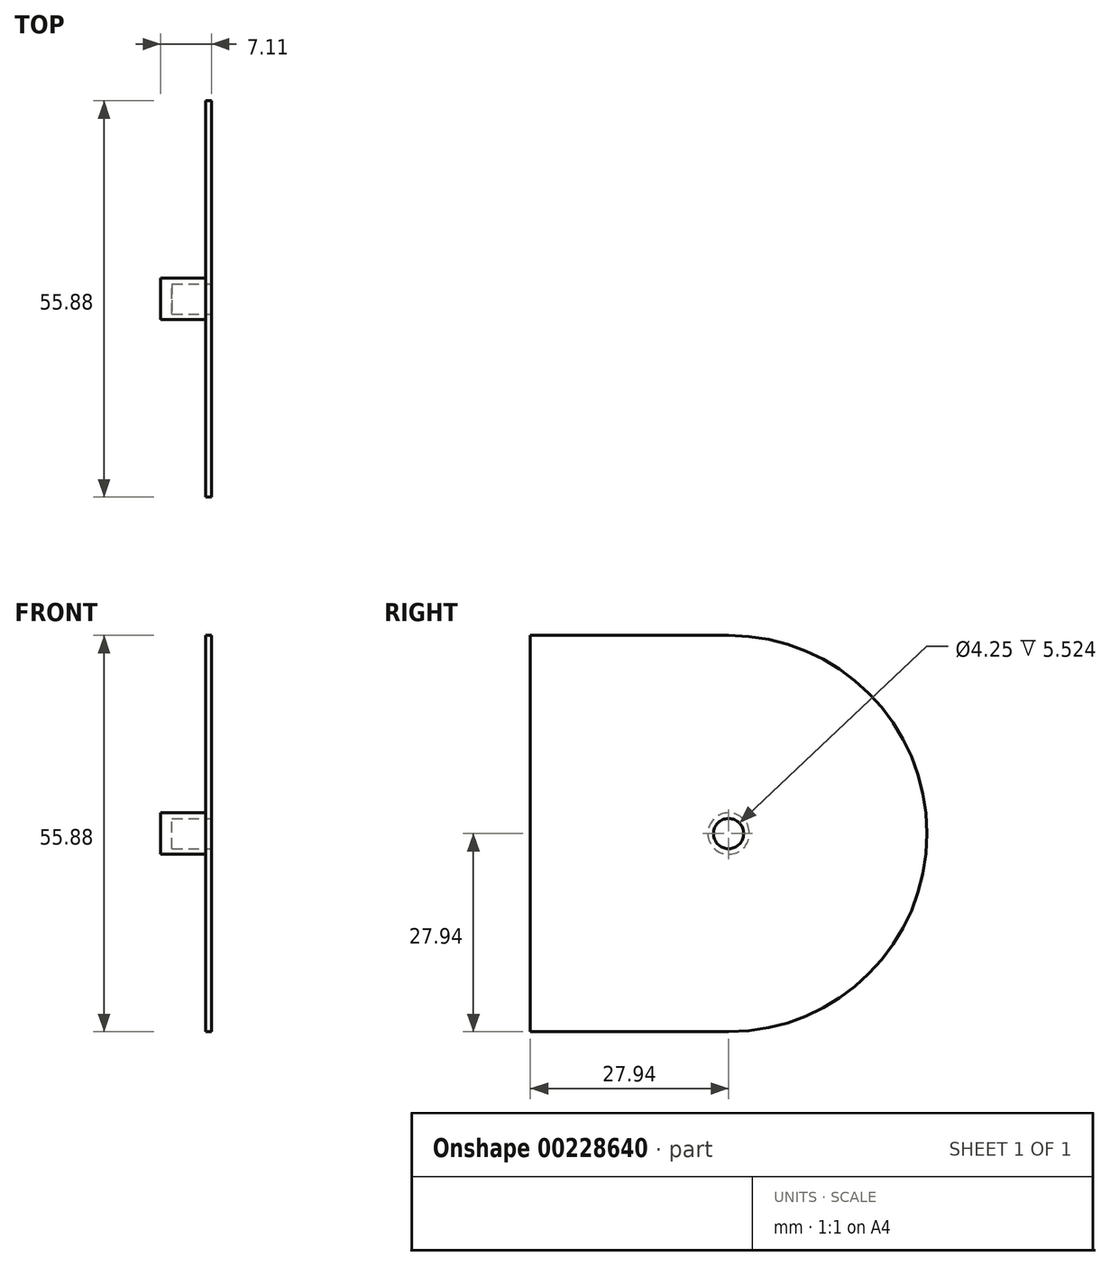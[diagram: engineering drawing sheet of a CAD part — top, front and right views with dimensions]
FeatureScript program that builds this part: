
annotation { "Feature Type Name" : "Feature", "Feature Type Description" : "" }
export const myFeature = defineFeature(function(context is Context, id is Id, definition is map)
    precondition{}
    {
        {
            var Q0;
            Q0=qCreatedBy(makeId("Right.planeOp"),FACE);
            var sketch = newSketch(context, id + "F0", { "sketchPlane" : qUnion([Q0])});
            skArc(sketch, "E0", {"start": v(0, -27.94) * mm, "mid": v(27.94, 0) * mm, "end": v(0, 27.94) * mm});
            skLineSegment(sketch, "E1", {"start": v(-27.94, 27.94) * mm, "end": v(-27.94, -27.94) * mm});
            skLineSegment(sketch, "E2", {"start": v(0, 27.94) * mm, "end": v(-27.94, 27.94) * mm});
            skLineSegment(sketch, "E3", {"start": v(0, -27.94) * mm, "end": v(-27.94, -27.94) * mm});
            skSolve(sketch);
        }
        {
            var Q0;
            Q0 = qSketchRegion(id + "F0", true);
            extrude(context, id + "F1", {"entities" : qUnion([Q0]), "depth" : 0.76 * mm, "offsetDistance" : 25.4 * mm});
        }
        {
            var Q0;
            Q0=makeQuery(id+"F1.opExtrude","CAP_FACE",FACE,{"disambiguationData":[OSD([sQuery(id+"F0.wireOp",EDGE,"vK9xomXJ-WcoS-fqkd-62vG-9ay9V5YrJpHx"),sQuery(id+"F0.wireOp",EDGE,"E0")])],"isStart":true});
            var sketch = newSketch(context, id + "F2", { "sketchPlane" : qUnion([Q0])});
            skCircle(sketch, "E4", {"center": v(0, 0) * mm, "radius": 2.92 * mm});
            skSolve(sketch);
        }
        {
            var Q0;
            Q0 = qSketchRegion(id + "F2", true);
            extrude(context, id + "F3", {"entities" : qUnion([Q0]), "operationType" : NewBodyOperationType.ADD, "depth" : 6.35 * mm, "offsetDistance" : 25.4 * mm});
        }
        {
            var Q0;
            Q0=makeQuery(id+"F1.opExtrude","CAP_FACE",FACE,{"disambiguationData":[OSD([sQuery(id+"F0.wireOp",EDGE,"E0")])],"isStart":false});
            var sketch = newSketch(context, id + "F4", { "sketchPlane" : qUnion([Q0])});
            skCircle(sketch, "E5", {"center": v(0, 0) * mm, "radius": 2.13 * mm});
            skSolve(sketch);
        }
        {
            var Q0;
            Q0 = qSketchRegion(id + "F4", true);
            extrude(context, id + "F5", {"entities" : qUnion([Q0]), "operationType" : NewBodyOperationType.REMOVE, "oppositeDirection" : true, "depth" : 5.52 * mm, "offsetDistance" : 25.4 * mm});
        }
    });
